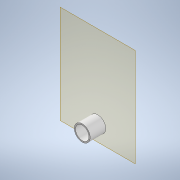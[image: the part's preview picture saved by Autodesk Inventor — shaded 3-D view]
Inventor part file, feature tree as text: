
AUTODESK INVENTOR PART (.ipt)
format: ipt  version: 2022 (Build 260153000, 153)  size: 101,888 bytes
history: native  units: mm
features: other x3, plane x1, extrude x1, sketch x1, reference x1
ambient origin geometry x8: Origin, YZ Plane, XZ Plane, XY Plane, X Axis, Y Axis, Z Axis, Center Point
bodies: Solid1 (feature_tree)
feature tree (7):
  plane  "Work Plane1"
  extrude  "Extrusion1"  Depth=10.0mm TaperAngle=0.0deg
  sketch  "Sketch1"  dims[d0=0.2mm d1=10.0mm d2=0.0mm]
  reference  "Reference1"
  other  "<userpath>\OneDrive - Imperial College London\ROBOICP MK2\solids feeder assembly.iam"
  other  "solids feeder assembly.iam"
  other  "screw_casing:1"
